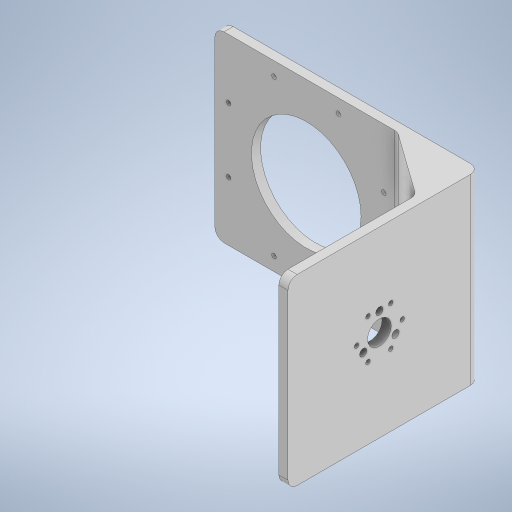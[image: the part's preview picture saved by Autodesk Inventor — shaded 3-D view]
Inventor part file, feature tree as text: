
AUTODESK INVENTOR PART (.ipt)
format: ipt  version: 2024.3 (Build 283343000, 343)  size: 359,424 bytes
history: native  units: mm
features: sketch x10, extrude x7, hole x3, other x1, fillet x1
ambient origin geometry x8: Origin, YZ Plane, XZ Plane, XY Plane, X Axis, Y Axis, Z Axis, Center Point
bodies: Body1 (feature_tree)
feature tree (22):
  other  "ソリッド1"
  extrude  "押し出し1"  Depth=97.0mm
  hole  "穴1"  [1 undecoded]
  extrude  "押し出し2"  Depth=50.0mm
  extrude  "押し出し3"  Depth=50.0mm
  extrude  "押し出し4"  Depth=50.0mm
  hole  "穴2"  [1 undecoded]
  hole  "穴3"  [1 undecoded]
  extrude  "押し出し5"  TaperAngle=22.5deg  [1 undecoded]
  extrude  "押し出し9"  Depth=80.0mm TaperAngle=360.0deg
  fillet  "フィレット2"  Radius=60.0mm
  extrude  "押し出し12"  Depth=5.0mm TaperAngle=0.0deg
  sketch  "スケッチ1"
  sketch  "スケッチ2"
  sketch  "スケッチ3"
  sketch  "スケッチ4"
  sketch  "スケッチ5"
  sketch  "スケッチ6"
  sketch  "スケッチ7"
  sketch  "スケッチ8"
  sketch  "スケッチ13"
  sketch  "スケッチ16"
note: 4 required parameter values undecoded (feature->parameter linkage not recoverable at this tier; creation-order binding heuristic only, values carry confidence <= 0.55)
